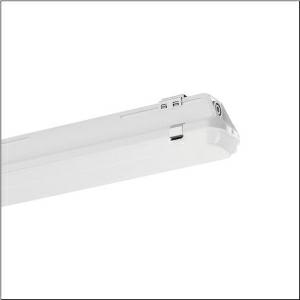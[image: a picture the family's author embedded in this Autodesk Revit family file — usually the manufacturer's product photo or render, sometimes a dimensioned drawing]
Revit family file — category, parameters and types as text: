
# Revit family: monsun_r__21_51fb10dp480b_f32f
name_source: partatom
category: Lighting Fixtures
units: mm (PartAtom-declared; Revit-internal decimal feet)

## family parameters
Cut with Voids When Loaded = No
Host = Face
Light Source = No
Part Type = Normal
Room Calculation Point = No
Round Connector Dimension = Use Diameter
Shared = No

## types (1)
- --- (1 x LED, 8090 lm, 54.4 W, 4000K)
    Apparent Load = 54 VA
    CIE Flux Codes = 47 77 93 94 100
    Color Rendering = 80
    Color Temperature = 4000K
    Default Elevation = 1800 mm
    Description = Monsun® 21, damp-proof luminaire, chain hanger, primary optical cover: enclosure, of PMMA, light emission: direct distribution, primary light characteristic: symmetric, installation type: suspended mounting, surface-mounted, horizontal mounting, vertical mounting, LED, rated luminous flux: 8.090lm, luminous efficacy: 149lm/W, light colour: 840, colour temperature: 4000K, control gear: ECG DALI, with terminal, 5-pole, max. 2.5mm², mains connection: 220..240V, AC, 50/60Hz, rated input power: 54W, housing, of glass-fibre reinforced polyester, uncoated, bright grey, length: 1.590mm, width: 90mm, height: 88mm, clip for enclosure, of stainless steel (V2A), ceiling mounting element, of stainless steel (V2A), chain hanger, of stainless steel (V2A), protection rating (complete): IP66, insulation class (complete): insulation class I (protective earthing), certification: CE, ENEC, VDE, UKCA, protection symbol: D, impact resistance: IK04, permissible operating ambient temperature: -25..+35°C, standard: EN 50419, EN 60598-2-1, corresponds to IFS (International Featured Standards) requirements for safety and quality in the food industry, for indoor or canopied outdoor use, no direct snow, no direct sun, no direct rain, packaging unit: 1 piece
    Height = 89 mm
    Lamp = 1 x LED
    Lamp Light Flux = 8090 lm
    Lamp Power = 54.4 W
    Lamp count = 1
    Length = 1590 mm
    Luminous efficacy = 149 lm/W
    Manufacturer = Siteco
    ModVariant = No
    Model = 51FB10DP480B
    Mounting Place = Ceiling
    Mounting Type = Pendant
    Number of Poles = 1
    OnlyDefault = Yes
    Power Factor = 1
    Product Name = Monsun® 21
    Product group = damp-proof luminaire | ceiling pendant
    ProductGroupID = 908
    Protection Class = Protection class I
    Protection Degree = IP 66
    RLX_Detail_Level = 1
    RlxData = <blob elided: 92373 chars, md5=dcb0850c>
    Socket = socket
    Standby Power = 0 W
    System Light Flux = 8090 lm
    System Power = 54 W
    Type Comments = factory setting: luminous flux: 100 % | dim-lin: 254 | 358 mA
    Type Image = l_1006717.jpg
    URL = http://relux.com
    VarID = @adj_125207
    Voltage = 0 V
    Weight = 0.00 kg
    Width = 90 mm

## geometry (parser evidence)
native form markers: Blend x4, Sweep x12
no freeform markers — native parametric forms only
